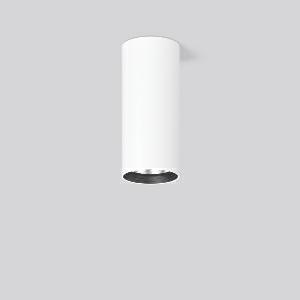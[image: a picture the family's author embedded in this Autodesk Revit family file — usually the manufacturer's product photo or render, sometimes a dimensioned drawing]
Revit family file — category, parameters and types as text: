
# Revit family: heledon_mini_a_931209_002_3_76_8706
name_source: partatom
category: Lighting Fixtures
units: mm (PartAtom-declared; Revit-internal decimal feet)

## family parameters
Cut with Voids When Loaded = No
Host = Face
Light Source = No
Part Type = Normal
Room Calculation Point = No
Round Connector Dimension = Use Diameter
Shared = No

## types (1)
- HELEDON mini A (1 x LED Modul 935, 3600 lm, 3500)
    Apparent Load = 29 VA
    Approval mark = CE
    CIE Flux Codes = 99 100 100 100 100
    Color Rendering = 92
    Color Temperature = 3500
    Default Elevation = 1800 mm
    Description = Series: HELEDON mini
Cylindrical surface-mounted downlight. Housing: die-cast aluminium, powder-coated. Internal ceiling frame polycarbonate with bayonet mounting. Black plastic ring and recessed LED to prevent glare from the side. Optical assembly with reflector made of MIRO-Silver with 98% total light reflection for outstanding efficiency - can be changed without tools. Best colour rendering index Ra>90. Suitable for Ceiling mounting. Easy installation with a separate ceiling frame with bayonet mounting and plug connection. Driver integrated. Connected via plug-in connector. High quality converter without flickering and stroboscopic effect. The following accessories can be mounted without use of tools: interchangeable lenses, decorative glasses, honeycomb louvre, clear and frosted diffusers, white interchangeable plastic ring. 
Colour: traffic white, matt (RAL 9016)
Diameter: 87 mm
Height: 197 mm
Lamp: LED
Socket: without socket
Colour temperature: 3500K
Colour rendering index (CRI): 92
System power: 29 W
Rated luminous flux: 3600 lm
Luminous efficiency: 124 lm/W
Control gear: Converter, dimmable, DALI
Protection class: I
Type of protection: IP 20
    Height = 197 mm
    Lamp = 1 x LED Modul 935
    Lamp Light Flux = 3600 lm
    Lamp count = 1
    Length = 87 mm
    Lifetime = 50000 h
    Luminous efficacy = 124 lm/W
    Manufacturer = RZB
    ModVariant = No
    Model = 931209.002.3.76
    Mounting Place = Ceiling
    Mounting Type = Surface mounted
    Number of Poles = 1
    OnlyDefault = Yes
    Power Factor = 1
    Product Name = HELEDON mini A
    Product group = Surface mounted downlights
    ProductGroupID = 302
    Protection Class = Protection class I
    Protection Degree = IP 20
    RLX_Detail_Level = 1
    RLX_Emergency_Light_Flux = 0 lm
    RLX_Emergency_Type = 0
    RLX_Emergency_Type_DB = No
    RlxData = <blob elided: 104281 chars, md5=3e6727ab>
    Socket = socket
    Standby Power = 0 W
    System Light Flux = 3600 lm
    System Power = 29 W
    Type Comments = Product without accessories
    Type Image = 931188.002.jpg
    URL = http://relux.com
    VarID = ---
    Voltage = 230 V
    Voltage Range = 220-240 V
    Weight = 0.00 kg
    Width = 0 mm  [stored 0 ft]

note: [stored X ft] marks values corroborated as IEEE doubles in the binary element streams (Revit-internal decimal feet)

## geometry (parser evidence)
native form markers: Blend x4, Sweep x9
no freeform markers — native parametric forms only
